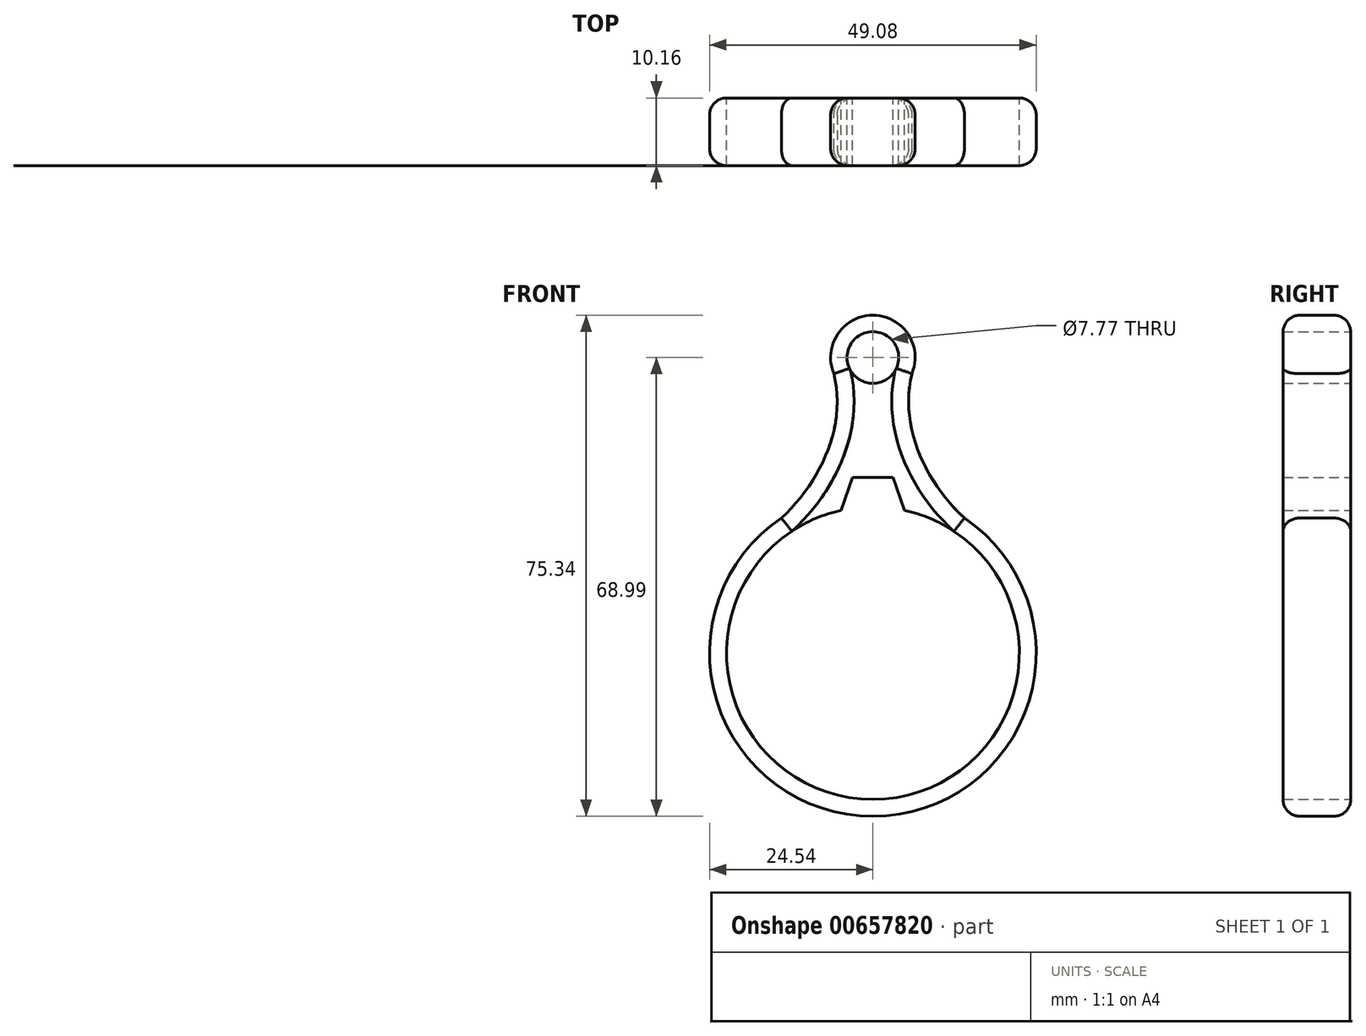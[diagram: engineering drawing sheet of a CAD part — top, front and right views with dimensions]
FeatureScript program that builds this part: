
annotation { "Feature Type Name" : "Feature", "Feature Type Description" : "" }
export const myFeature = defineFeature(function(context is Context, id is Id, definition is map)
    precondition{}
    {
        {
            var Q0;
            Q0=qCreatedBy(makeId("Front.planeOp"),FACE);
            var sketch = newSketch(context, id + "F0", { "sketchPlane" : qUnion([Q0])});
            skCircle(sketch, "E0", {"center": v(0, 0) * mm, "radius": 22 * mm});
            skCircle(sketch, "E1", {"center": v(0, 0) * mm, "radius": 24.54 * mm});
            skLineSegment(sketch, "E2", {"start": v(0, 0) * mm, "end": v(0, 44.45) * mm});
            skCircle(sketch, "E3", {"center": v(0, 44.45) * mm, "radius": 6.35 * mm});
            skFitSpline(sketch, "E4", {"points": [v(-5.86, 42) * mm, v(-13.76, 20.32) * mm], "startDerivative": vector(6.03, -24.04) * mm, "endDerivative": vector(-16.99, -15.51) * mm});
            skFitSpline(sketch, "E5.MirrorCS", {"points": [v(5.86, 42) * mm, v(13.76, 20.32) * mm], "startDerivative": vector(-6.03, -24.04) * mm, "endDerivative": vector(16.99, -15.51) * mm});
            skLineSegment(sketch, "E6", {"start": v(-4.77, 21.47) * mm, "end": v(-3.06, 26.4) * mm});
            skLineSegment(sketch, "E7", {"start": v(-3.06, 26.4) * mm, "end": v(0, 26.4) * mm});
            skLineSegment(sketch, "E8.MirrorCS", {"start": v(3.06, 26.4) * mm, "end": v(0, 26.4) * mm});
            skLineSegment(sketch, "E9.MirrorCS", {"start": v(4.77, 21.47) * mm, "end": v(3.06, 26.4) * mm});
            skCircle(sketch, "E10", {"center": v(0, 44.45) * mm, "radius": 3.88 * mm});
            skSolve(sketch);
        }
        {
            var Q0;
            {var subQ0=sQuery(id+"F0.wireOp",EDGE,"E3");var subQ1=makeQuery(id+"F0.imprint","INTERSECT",VERTEX,{"derivedFrom":[subQ0,sQuery(id+"F0.wireOp",EDGE,"E4")]});Q0=makeQuery(id+"F0.imprint","IMPRINT",FACE,{"disambiguationData":[TD([[makeQuery(id+"F0.imprint","IMPRINT",EDGE,{"disambiguationData":[TD([[subQ1,-1.0]])],"derivedFrom":subQ0}),1.0]])]});}
            var Q1;
            {var subQ0=sQuery(id+"F0.wireOp",EDGE,"G6ikKppZ-whfM-rzma-JBQc-gByEVGELcU4d");Q1=makeQuery(id+"F0.imprint","IMPRINT",FACE,{"disambiguationData":[TD([[makeQuery(id+"F0.imprint","IMPRINT",EDGE,{"derivedFrom":subQ0}),-1.0]])]});}
            var Q2;
            {var subQ0=sQuery(id+"F0.wireOp",EDGE,"E4");Q2=makeQuery(id+"F0.imprint","IMPRINT",FACE,{"disambiguationData":[TD([[makeQuery(id+"F0.imprint","IMPRINT",EDGE,{"derivedFrom":subQ0}),1.0]])]});}
            var Q3;
            {var subQ5=sQuery(id+"F0.wireOp",EDGE,"E9.MirrorCS");var subQ7=sQuery(id+"F0.wireOp",EDGE,"E0");var subQ8=makeQuery(id+"F0.imprint","INTERSECT",VERTEX,{"derivedFrom":[subQ7,subQ5]});Q3=makeQuery(id+"F0.imprint","IMPRINT",FACE,{"disambiguationData":[TD([[makeQuery(id+"F0.imprint","IMPRINT",EDGE,{"disambiguationData":[TD([[subQ8,1.0]])],"derivedFrom":subQ7}),-1.0]])]});}
            var Q4;
            {var subQ0=sQuery(id+"F0.wireOp",EDGE,"E8.MirrorCS");Q4=makeQuery(id+"F0.imprint","IMPRINT",FACE,{"disambiguationData":[TD([[makeQuery(id+"F0.imprint","IMPRINT",EDGE,{"derivedFrom":subQ0}),-1.0]])]});}
            var Q5;
            {var subQ0=sQuery(id+"F0.wireOp",EDGE,"E7");Q5=makeQuery(id+"F0.imprint","IMPRINT",FACE,{"disambiguationData":[TD([[makeQuery(id+"F0.imprint","IMPRINT",EDGE,{"derivedFrom":subQ0}),1.0]])]});}
            var Q6;
            {var subQ0=sQuery(id+"F0.wireOp",EDGE,"E6");var subQ1=sQuery(id+"F0.wireOp",EDGE,"E0");var subQ2=makeQuery(id+"F0.imprint","INTERSECT",VERTEX,{"derivedFrom":[subQ1,subQ0]});Q6=makeQuery(id+"F0.imprint","IMPRINT",FACE,{"disambiguationData":[TD([[makeQuery(id+"F0.imprint","IMPRINT",EDGE,{"disambiguationData":[TD([[subQ2,-1.0]])],"derivedFrom":subQ1}),-1.0]])]});}
            extrude(context, id + "F1", {"entities" : qUnion([Q0, Q1, Q2, Q3, Q4, Q5, Q6]), "depth" : 10.16 * mm, "offsetDistance" : 25.4 * mm});
        }
        {
            var Q0;
            Q0=makeQuery(id+"F1.opExtrude","CAP_EDGE",EDGE,{"disambiguationData":[OSD([sQuery(id+"F0.wireOp",EDGE,"E3")])],"isStart":true});
            var Q1;
            Q1=makeQuery(id+"F1.opExtrude","CAP_EDGE",EDGE,{"disambiguationData":[OSD([sQuery(id+"F0.wireOp",EDGE,"E4")])],"isStart":true});
            var Q2;
            Q2=makeQuery(id+"F1.opExtrude","CAP_EDGE",EDGE,{"disambiguationData":[OSD([sQuery(id+"F0.wireOp",EDGE,"E5.MirrorCS")])],"isStart":true});
            var Q3;
            Q3=makeQuery(id+"F1.opExtrude","CAP_EDGE",EDGE,{"disambiguationData":[OSD([sQuery(id+"F0.wireOp",EDGE,"E1")])],"isStart":true});
            var Q4;
            Q4=makeQuery(id+"F1.opExtrude","CAP_EDGE",EDGE,{"disambiguationData":[OSD([sQuery(id+"F0.wireOp",EDGE,"E3")])],"isStart":false});
            var Q5;
            Q5=makeQuery(id+"F1.opExtrude","CAP_EDGE",EDGE,{"disambiguationData":[OSD([sQuery(id+"F0.wireOp",EDGE,"E4")])],"isStart":false});
            var Q6;
            Q6=makeQuery(id+"F1.opExtrude","CAP_EDGE",EDGE,{"disambiguationData":[OSD([sQuery(id+"F0.wireOp",EDGE,"E1")])],"isStart":false});
            var Q7;
            Q7=makeQuery(id+"F1.opExtrude","CAP_EDGE",EDGE,{"disambiguationData":[OSD([sQuery(id+"F0.wireOp",EDGE,"E5.MirrorCS")])],"isStart":false});
            fillet(context, id + "F2", {"entities" : qUnion([Q0, Q1, Q2, Q3, Q4, Q5, Q6, Q7]), "radius" : 2.54 * mm, "tangentPropagation" : true, "allowEdgeOverflow" : false});
        }
    });
